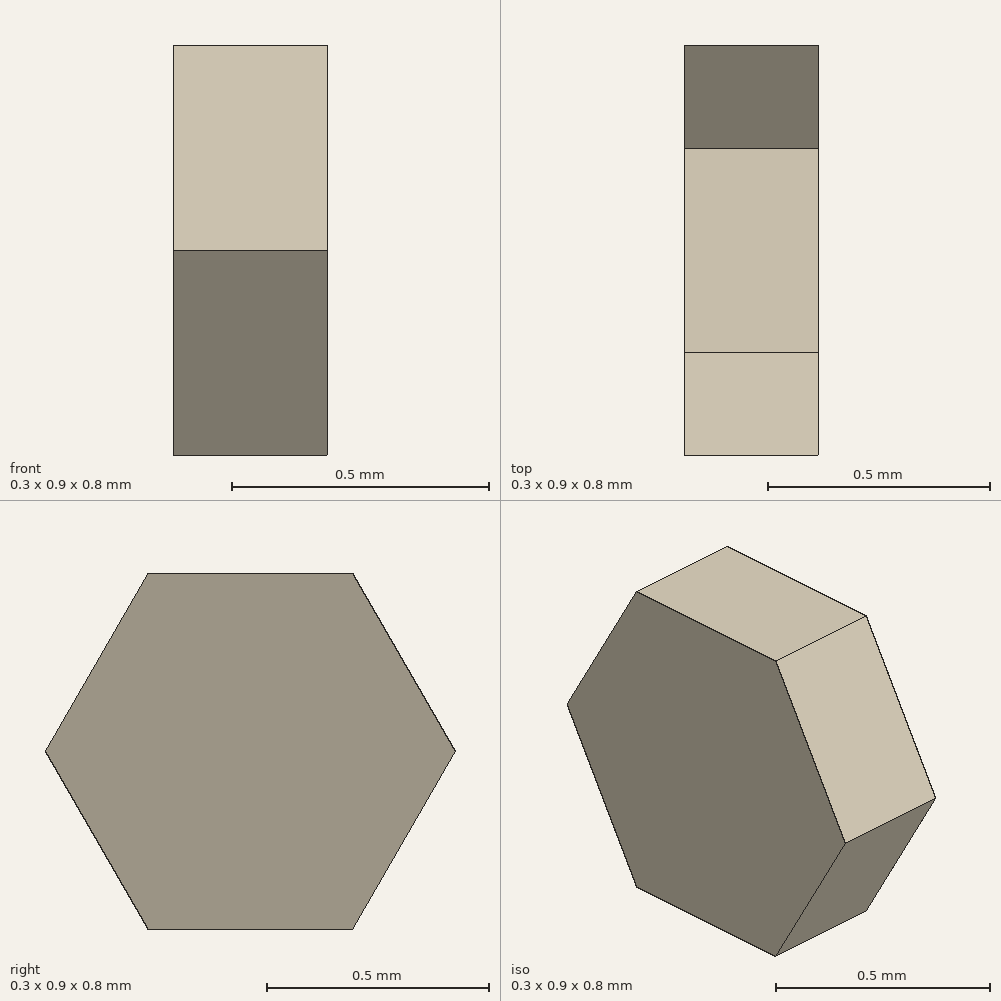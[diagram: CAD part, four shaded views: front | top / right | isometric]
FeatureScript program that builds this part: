
annotation { "Feature Type Name" : "Feature", "Feature Type Description" : "" }
export const myFeature = defineFeature(function(context is Context, id is Id, definition is map)
    precondition{}
    {
        {
            var Q0;
            Q0=qCreatedBy(makeId("Right.planeOp"),FACE);
            var sketch = newSketch(context, id + "F0", { "sketchPlane" : qUnion([Q0])});
            skCircle(sketch, "E0.cCircle", {"center": v(0, 0) * mm, "radius": 0.4 * mm, "construction": true});
            skLineSegment(sketch, "E0.0", {"start": v(-0.23, 0.4) * mm, "end": v(0.23, 0.4) * mm});
            skLineSegment(sketch, "E0.1", {"start": v(0.23, 0.4) * mm, "end": v(0.46, 0) * mm});
            skLineSegment(sketch, "E0.2", {"start": v(0.46, 0) * mm, "end": v(0.23, -0.4) * mm});
            skLineSegment(sketch, "E0.3", {"start": v(0.23, -0.4) * mm, "end": v(-0.23, -0.4) * mm});
            skLineSegment(sketch, "E0.4", {"start": v(-0.23, -0.4) * mm, "end": v(-0.46, 0) * mm});
            skLineSegment(sketch, "E0.5", {"start": v(-0.46, 0) * mm, "end": v(-0.23, 0.4) * mm});
            skPoint(sketch, "E0.0.midPoint", {"position": v(0, 0.4) * mm});
            skSolve(sketch);
        }
        {
            var Q0;
            Q0 = qSketchRegion(id + "F0", true);
            extrude(context, id + "F1", {"entities" : qUnion([Q0]), "depth" : .3 * mm, "offsetDistance" : 25 * mm});
        }
    });
